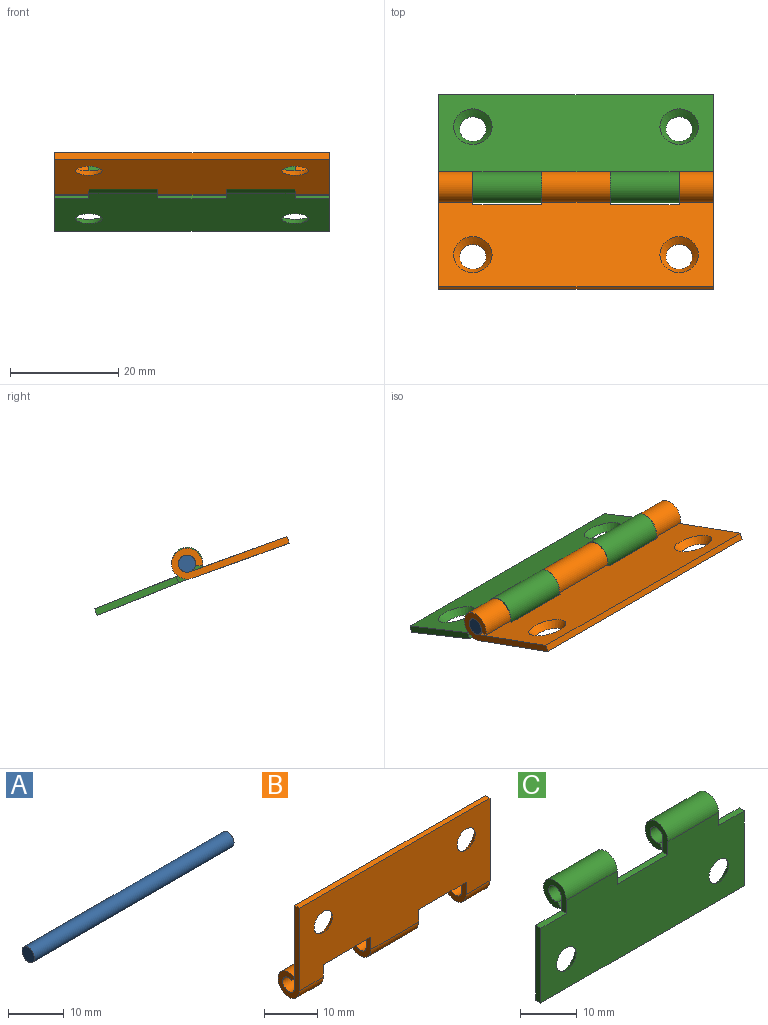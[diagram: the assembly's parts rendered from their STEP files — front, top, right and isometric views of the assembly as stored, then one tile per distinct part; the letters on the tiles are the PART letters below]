
ASSEMBLY  parts=3 mates=2
PART A: 3 faces, bbox 50.8x3.2x3.2 mm
  f0: cylinder r=1.59mm len=50.8mm, axis (-1,0,0), area 506.7mm2, adj f1,f2
  f1: plane 3.18x3.18mm, normal (1,0,0), area 7.9mm2, adj f0
  f2: plane 3.18x3.18mm, normal (-1,0,0), area 7.9mm2, adj f0
PART B: 22 faces, bbox 50.8x5.7x21.9 mm
  f0: cylinder r=2.86mm len=6.35mm, axis (-1,0,0), area 94.7mm2, adj f1,f11,f16,f20
  f1: plane 6.35x1.11mm, normal (0,-0.87,-0.49), area 8.1mm2, adj f0,f2,f16,f20
  f2: cylinder r=1.59mm len=6.35mm, axis (-1,0,0), area 52.6mm2, adj f1,f3,f16,f20
  f3: plane 50.8x19.05mm, normal (0,1,0), area 816.3mm2, adj f2,f6,f9,f10,f12,f13,f14,f15
  f4: cylinder r=2.86mm len=12.7mm, axis (-1,0,0), area 189.4mm2, adj f5,f11,f13,f17
  f5: plane 12.7x1.11mm, normal (0,-0.87,-0.49), area 16.1mm2, adj f4,f6,f13,f17
  f6: cylinder r=1.59mm len=12.7mm, axis (-1,0,0), area 105.2mm2, adj f3,f5,f13,f17
  f7: cylinder r=2.86mm len=6.35mm, axis (-1,0,0), area 94.7mm2, adj f8,f11,f12,f14
  f8: plane 6.35x1.11mm, normal (0,-0.87,-0.49), area 8.1mm2, adj f7,f9,f12,f14
  f9: cylinder r=1.59mm len=6.35mm, axis (-1,0,0), area 52.6mm2, adj f3,f8,f12,f14
  f10: plane 50.8x1.27mm, normal (0,0,1), area 64.5mm2, adj f3,f11,f12,f20
  f11: plane 50.8x19.05mm, normal (0,-1,0), area 857.8mm2, adj f0,f4,f7,f10,f12,f13,f14,f15
  f12: plane 21.91x5.72mm, normal (1,0,0), area 38.9mm2, adj f3,f7,f8,f9,f10,f11
  f13: plane 5.72x5.72mm, normal (1,0,0), area 18.4mm2, adj f3,f4,f5,f6,f11,f15
  f14: plane 5.72x5.72mm, normal (-1,0,0), area 18.4mm2, adj f3,f7,f8,f9,f11,f15
  f15: plane 12.7x1.27mm, normal (0,0,-1), area 16.1mm2, adj f3,f11,f13,f14
  f16: plane 5.72x5.72mm, normal (1,0,0), area 18.4mm2, adj f0,f1,f2,f3,f11,f18
  f17: plane 5.72x5.72mm, normal (-1,0,0), area 18.4mm2, adj f3,f4,f5,f6,f11,f18
  f18: plane 12.7x1.27mm, normal (0,0,-1), area 16.1mm2, adj f3,f11,f16,f17
  f19: cone r=3.54mm half-angle=41deg, axis (0,1,0), area 31.6mm2, adj f3,f11
  f20: plane 21.91x5.72mm, normal (-1,0,0), area 38.9mm2, adj f0,f1,f2,f3,f10,f11
  f21: cone r=3.54mm half-angle=41deg, axis (0,1,0), area 31.6mm2, adj f3,f11
PART C: 20 faces, bbox 50.8x5.7x21.9 mm
  f0: plane 50.8x1.27mm, normal (0,0,-1), area 64.5mm2, adj f1,f7,f10,f18
  f1: plane 50.8x19.05mm, normal (0,1,0), area 816.3mm2, adj f0,f2,f5,f8,f10,f11,f12,f13
  f2: plane 6.35x1.27mm, normal (0,0,1), area 8.1mm2, adj f1,f7,f11,f18
  f3: cylinder r=2.86mm len=12.7mm, axis (-1,0,0), area 189.4mm2, adj f7,f9,f14,f15
  f4: cylinder r=2.86mm len=12.7mm, axis (-1,0,0), area 189.4mm2, adj f6,f7,f11,f13
  f5: cylinder r=1.59mm len=12.7mm, axis (-1,0,0), area 105.2mm2, adj f1,f6,f11,f13
  f6: plane 12.7x1.11mm, normal (0,-0.87,0.49), area 16.1mm2, adj f4,f5,f11,f13
  f7: plane 50.8x19.05mm, normal (0,-1,0), area 857.8mm2, adj f0,f2,f3,f4,f10,f11,f12,f13
  f8: cylinder r=1.59mm len=12.7mm, axis (-1,0,0), area 105.2mm2, adj f1,f9,f14,f15
  f9: plane 12.7x1.11mm, normal (0,-0.87,0.49), area 16.1mm2, adj f3,f8,f14,f15
  f10: plane 16.19x1.27mm, normal (1,0,0), area 20.6mm2, adj f0,f1,f7,f16
  f11: plane 5.72x5.72mm, normal (-1,0,0), area 18.4mm2, adj f1,f2,f4,f5,f6,f7
  f12: plane 12.7x1.27mm, normal (0,0,1), area 16.1mm2, adj f1,f7,f13,f14
  f13: plane 5.72x5.72mm, normal (1,0,0), area 18.4mm2, adj f1,f4,f5,f6,f7,f12
  f14: plane 5.72x5.72mm, normal (-1,0,0), area 18.4mm2, adj f1,f3,f7,f8,f9,f12
  f15: plane 5.72x5.72mm, normal (1,0,0), area 18.4mm2, adj f1,f3,f7,f8,f9,f16
  f16: plane 6.35x1.27mm, normal (0,0,1), area 8.1mm2, adj f1,f7,f10,f15
  f17: cone r=3.54mm half-angle=41deg, axis (0,1,0), area 31.6mm2, adj f1,f7
  f18: plane 16.19x1.27mm, normal (-1,0,0), area 20.6mm2, adj f0,f1,f2,f7
  f19: cone r=3.54mm half-angle=41deg, axis (0,1,0), area 31.6mm2, adj f1,f7
PLACE A at identity fixed
PLACE B rot(axis=(1,0,0),70.1deg) t=(0,0,0)mm
PLACE C rot(axis=(1,0,0),68.3deg) t=(0,-0.05,0.16)mm
MATE revolute C.f11 <-> A.f0  axis (-1,0,0) through (25.4,0,0)mm
MATE revolute B.f0 <-> A.f0  axis (-1,0,0) through (19.05,0,0)mm
